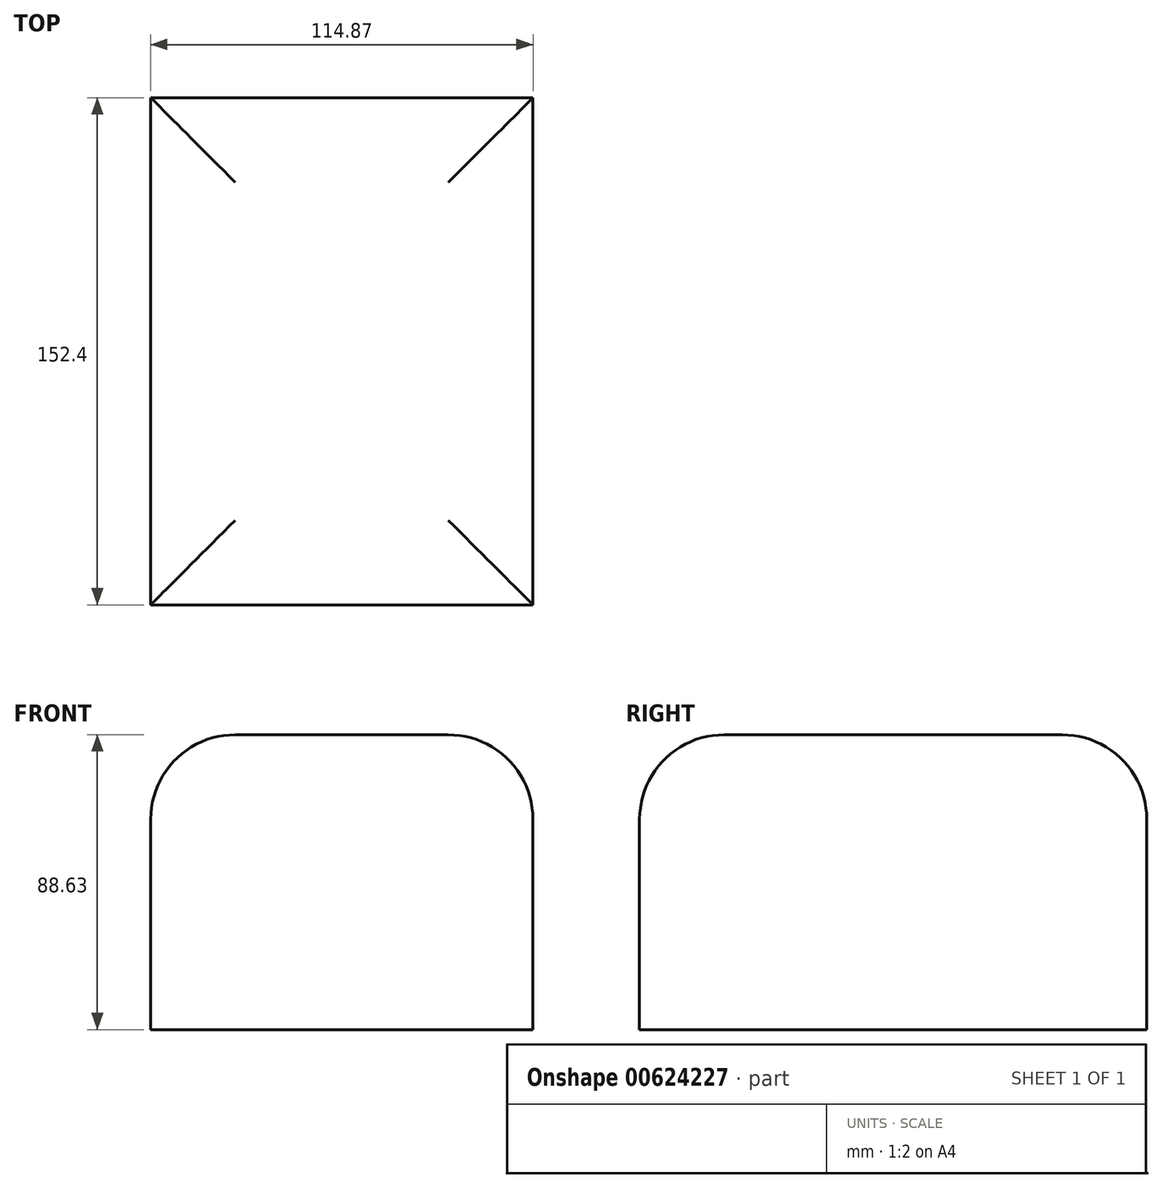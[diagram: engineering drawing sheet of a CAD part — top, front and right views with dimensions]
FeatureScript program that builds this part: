
annotation { "Feature Type Name" : "Feature", "Feature Type Description" : "" }
export const myFeature = defineFeature(function(context is Context, id is Id, definition is map)
    precondition{}
    {
        {
            var Q0;
            Q0=qCreatedBy(makeId("Front.planeOp"),FACE);
            var sketch = newSketch(context, id + "F0", { "sketchPlane" : qUnion([Q0])});
            skLineSegment(sketch, "E0.bottom", {"start": v(-52.75, 49.19) * mm, "end": v(62.12, 49.19) * mm});
            skLineSegment(sketch, "E0.top", {"start": v(-52.75, -39.44) * mm, "end": v(62.12, -39.44) * mm});
            skLineSegment(sketch, "E0.left", {"start": v(-52.75, 49.19) * mm, "end": v(-52.75, -39.44) * mm});
            skLineSegment(sketch, "E0.right", {"start": v(62.12, 49.19) * mm, "end": v(62.12, -39.44) * mm});
            skSolve(sketch);
        }
        {
            var Q0;
            Q0 = qSketchRegion(id + "F0", true);
            extrude(context, id + "F1", {"entities" : qUnion([Q0]), "depth" : 152.4 * mm, "offsetDistance" : 25.4 * mm});
        }
        {
            var Q0;
            Q0=makeQuery(id+"F1.opExtrude","SWEPT_FACE",FACE,{"disambiguationData":[OSD([sQuery(id+"F0.wireOp",EDGE,"E0.bottom")])]});
            fillet(context, id + "F2", {"entities" : qUnion([Q0]), "radius" : 25.4 * mm, "tangentPropagation" : true, "allowEdgeOverflow" : false});
        }
    });
